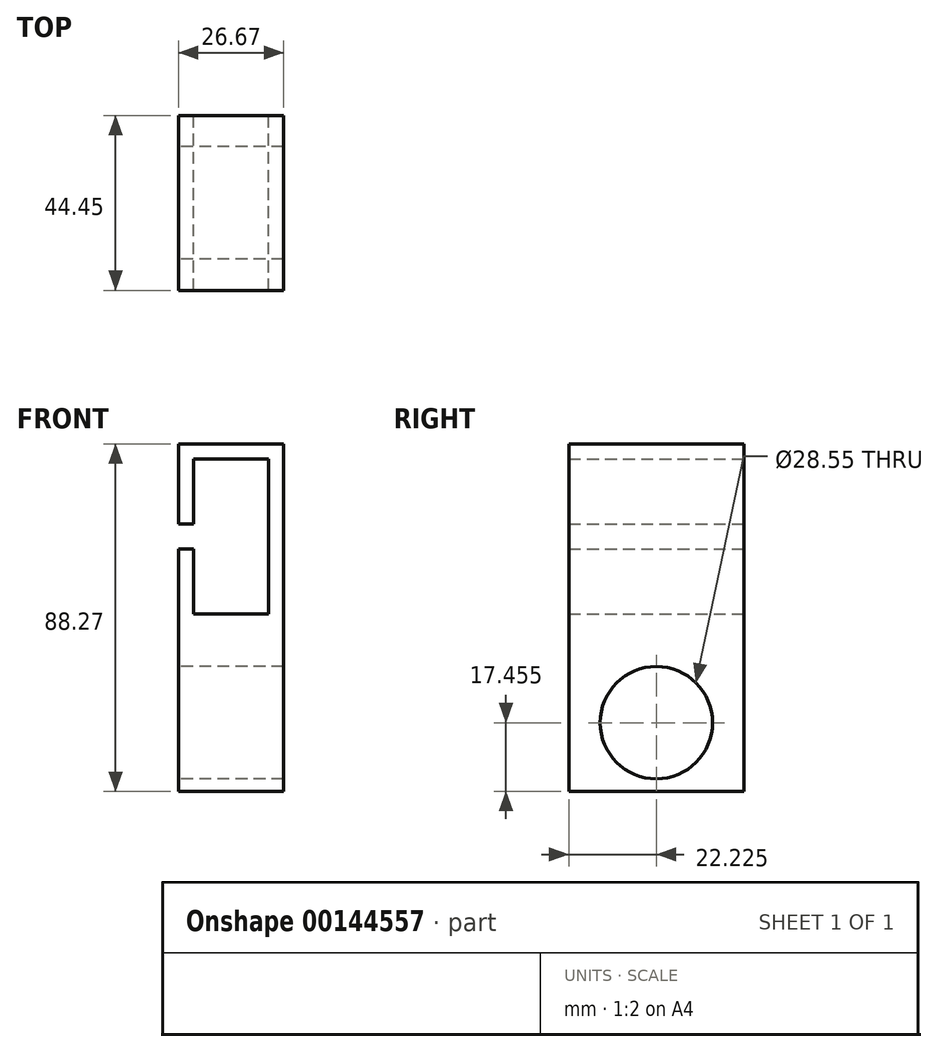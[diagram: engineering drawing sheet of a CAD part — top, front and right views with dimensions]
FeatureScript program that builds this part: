
annotation { "Feature Type Name" : "Feature", "Feature Type Description" : "" }
export const myFeature = defineFeature(function(context is Context, id is Id, definition is map)
    precondition{}
    {
        {
            var Q0;
            Q0=qCreatedBy(makeId("Front.planeOp"),FACE);
            var sketch = newSketch(context, id + "F0", { "sketchPlane" : qUnion([Q0])});
            skLineSegment(sketch, "E0", {"start": v(0, 0) * mm, "end": v(0, 19.05) * mm});
            skLineSegment(sketch, "E1", {"start": v(0, 19.05) * mm, "end": v(-19.05, 19.05) * mm});
            skLineSegment(sketch, "E2", {"start": v(-19.05, 19.05) * mm, "end": v(-19.05, 2.54) * mm});
            skLineSegment(sketch, "E3", {"start": v(-19.05, -3.8) * mm, "end": v(-19.05, -20.32) * mm});
            skLineSegment(sketch, "E4", {"start": v(-19.05, -20.32) * mm, "end": v(0, -20.32) * mm});
            skLineSegment(sketch, "E5", {"start": v(0, -20.32) * mm, "end": v(0, 0) * mm});
            skLineSegment(sketch, "E6", {"start": v(-9.53, 22.86) * mm, "end": v(-22.86, 22.86) * mm});
            skLineSegment(sketch, "E7", {"start": v(-22.86, 22.86) * mm, "end": v(-22.86, -24.13) * mm});
            skLineSegment(sketch, "E8", {"start": v(-22.86, -24.13) * mm, "end": v(3.81, -24.13) * mm});
            skLineSegment(sketch, "E9", {"start": v(3.81, -24.13) * mm, "end": v(3.8, 22.86) * mm});
            skLineSegment(sketch, "E10", {"start": v(3.8, 22.86) * mm, "end": v(-22.86, 22.86) * mm});
            skLineSegment(sketch, "E11", {"start": v(-19.05, 2.54) * mm, "end": v(-22.86, 2.54) * mm});
            skLineSegment(sketch, "E12", {"start": v(-22.86, 2.54) * mm, "end": v(-22.86, -3.8) * mm});
            skLineSegment(sketch, "E13", {"start": v(-22.86, -3.8) * mm, "end": v(-19.05, -3.8) * mm});
            skSolve(sketch);
        }
        {
            var Q0;
            Q0=makeQuery(id+"F0.imprint","IMPRINT",FACE,{"disambiguationData":[TD([[makeQuery(id+"F0.imprint","IMPRINT",EDGE,{"derivedFrom":sQuery(id+"F0.wireOp",EDGE,"E0")}),-1.0]])]});
            extrude(context, id + "F1", {"entities" : qUnion([Q0]), "depth" : 44.45 * mm, "offsetDistance" : 25.4 * mm});
        }
        {
            var Q0;
            Q0=makeQuery(id+"F1.opExtrude","SWEPT_FACE",FACE,{"disambiguationData":[OSD([sQuery(id+"F0.wireOp",EDGE,"E8")])]});
            extrude(context, id + "F2", {"entities" : qUnion([Q0]), "operationType" : NewBodyOperationType.ADD, "depth" : 41.27 * mm, "offsetDistance" : 25.4 * mm});
        }
        {
            var Q0;
            {var subQ0=sQuery(id+"F0.wireOp",EDGE,"E8");var subQ1=sQuery(id+"F0.wireOp",EDGE,"E7");Q0=makeQuery(id+"F2.boolean.opBoolean","MERGE",FACE,{"derivedFrom":[makeQuery(id+"F1.opExtrude","SWEPT_FACE",FACE,{"disambiguationData":[OSD([subQ1]),TDD([makeQuery(id+"F0.imprint","IMPRINT",EDGE,{"disambiguationData":[TD([[makeQuery(id+"F0.imprint","INTERSECT",VERTEX,{"derivedFrom":[subQ1,subQ0]}),1.0]])],"derivedFrom":subQ1})])]}),makeQuery(id+"F2.opExtrude","SWEPT_FACE",FACE,{"disambiguationData":[OSD([subQ1,subQ0])]})]});}
            var sketch = newSketch(context, id + "F3", { "sketchPlane" : qUnion([Q0])});
            skLineSegment(sketch, "E14", {"start": v(22.23, -65.4) * mm, "end": v(22.23, -62.23) * mm});
            skLineSegment(sketch, "E15", {"start": v(22.23, -62.23) * mm, "end": v(22.23, -33.68) * mm});
            skCircle(sketch, "E16", {"center": v(22.23, -47.96) * mm, "radius": 14.27 * mm});
            skSolve(sketch);
        }
        {
            var Q0;
            {var subQ0=sQuery(id+"F3.wireOp",EDGE,"E15");Q0=makeQuery(id+"F3.imprint","IMPRINT",FACE,{"disambiguationData":[TD([[makeQuery(id+"F3.imprint","IMPRINT",EDGE,{"derivedFrom":subQ0}),1.0]])]});}
            var Q1;
            {var subQ0=sQuery(id+"F3.wireOp",EDGE,"E15");Q1=makeQuery(id+"F3.imprint","IMPRINT",FACE,{"disambiguationData":[TD([[makeQuery(id+"F3.imprint","IMPRINT",EDGE,{"derivedFrom":subQ0}),-1.0]])]});}
            extrude(context, id + "F4", {"entities" : qUnion([Q0, Q1]), "operationType" : NewBodyOperationType.REMOVE, "oppositeDirection" : true, "depth" : 38.1 * mm, "offsetDistance" : 25.4 * mm});
        }
    });
